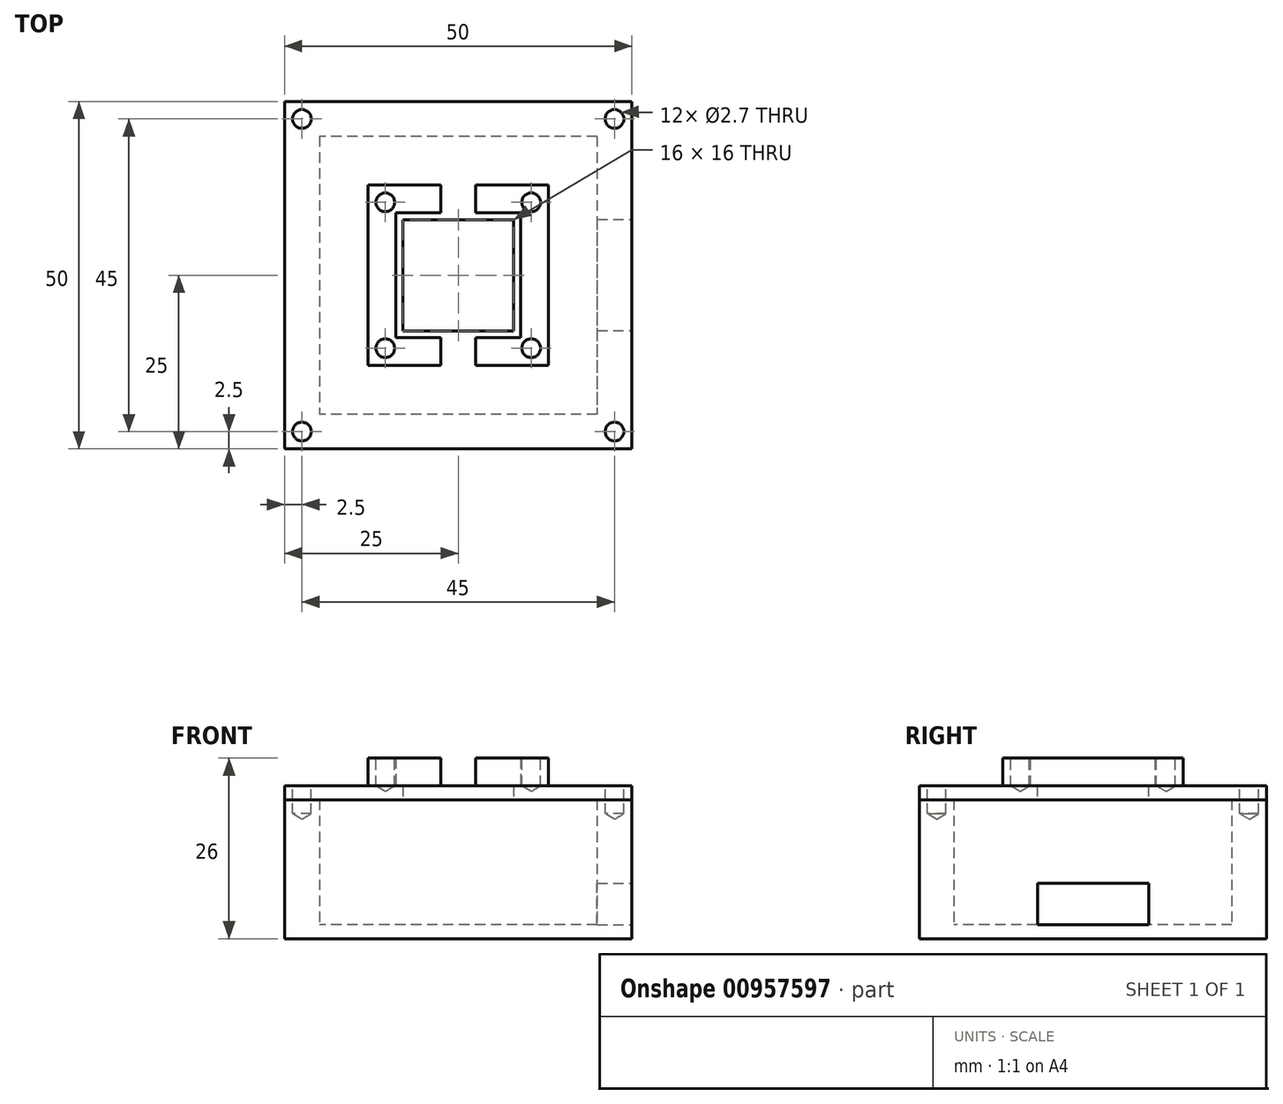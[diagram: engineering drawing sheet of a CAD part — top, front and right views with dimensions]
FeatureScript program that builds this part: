
annotation { "Feature Type Name" : "Feature", "Feature Type Description" : "" }
export const myFeature = defineFeature(function(context is Context, id is Id, definition is map)
    precondition{}
    {
        {
            var Q0;
            Q0=qCreatedBy(makeId("Top.planeOp"),FACE);
            var sketch = newSketch(context, id + "F0", { "sketchPlane" : qUnion([Q0])});
            skLineSegment(sketch, "E0.bottom", {"start": v(20, 20) * mm, "end": v(-20, 20) * mm});
            skLineSegment(sketch, "E0.top", {"start": v(20, -20) * mm, "end": v(-20, -20) * mm});
            skLineSegment(sketch, "E0.left", {"start": v(20, 20) * mm, "end": v(20, -20) * mm});
            skLineSegment(sketch, "E0.right", {"start": v(-20, 20) * mm, "end": v(-20, -20) * mm});
            skPoint(sketch, "E0.middle", {"position": v(0, 0) * mm});
            skLineSegment(sketch, "E1.bottom", {"start": v(25, -25) * mm, "end": v(-25, -25) * mm});
            skLineSegment(sketch, "E1.top", {"start": v(25, 25) * mm, "end": v(-25, 25) * mm});
            skLineSegment(sketch, "E1.left", {"start": v(25, -25) * mm, "end": v(25, 25) * mm});
            skLineSegment(sketch, "E1.right", {"start": v(-25, -25) * mm, "end": v(-25, 25) * mm});
            skSolve(sketch);
        }
        {
            var Q0;
            Q0=makeQuery(id+"F0.imprint","IMPRINT",FACE,{"disambiguationData":[TD([[makeQuery(id+"F0.imprint","IMPRINT",EDGE,{"derivedFrom":sQuery(id+"F0.wireOp",EDGE,"E0.bottom")}),-1.0]])]});
            extrude(context, id + "F1", {"entities" : qUnion([Q0]), "depth" : 18 * mm, "offsetDistance" : 25 * mm});
        }
        {
            var Q0;
            Q0=makeQuery(id+"F0.imprint","IMPRINT",FACE,{"disambiguationData":[TD([[makeQuery(id+"F0.imprint","IMPRINT",EDGE,{"derivedFrom":sQuery(id+"F0.wireOp",EDGE,"E0.bottom")}),-1.0]])]});
            var Q1;
            Q1=makeQuery(id+"F0.imprint","IMPRINT",FACE,{"disambiguationData":[TD([[makeQuery(id+"F0.imprint","IMPRINT",EDGE,{"derivedFrom":sQuery(id+"F0.wireOp",EDGE,"E0.bottom")}),1.0]])]});
            extrude(context, id + "F2", {"entities" : qUnion([Q0, Q1]), "operationType" : NewBodyOperationType.ADD, "oppositeDirection" : true, "depth" : 2 * mm, "offsetDistance" : 25 * mm});
        }
        {
            var Q0;
            {var subQ0=sQuery(id+"F0.wireOp",EDGE,"E1.left");Q0=makeQuery(id+"F2.boolean.opBoolean","MERGE",FACE,{"derivedFrom":[makeQuery(id+"F1.opExtrude","SWEPT_FACE",FACE,{"disambiguationData":[OSD([subQ0])]}),makeQuery(id+"F2.opExtrude","SWEPT_FACE",FACE,{"disambiguationData":[OSD([subQ0])]})]});}
            var sketch = newSketch(context, id + "F3", { "sketchPlane" : qUnion([Q0])});
            skLineSegment(sketch, "E2.bottom", {"start": v(-7.98, 6) * mm, "end": v(8.02, 6) * mm});
            skLineSegment(sketch, "E2.top", {"start": v(-7.98, 0) * mm, "end": v(8.02, 0) * mm});
            skLineSegment(sketch, "E2.left", {"start": v(-7.98, 6) * mm, "end": v(-7.98, 0) * mm});
            skLineSegment(sketch, "E2.right", {"start": v(8.02, 6) * mm, "end": v(8.02, 0) * mm});
            skLineSegment(sketch, "E3", {"start": v(-7.98, -2) * mm, "end": v(-7.98, 8) * mm, "construction": true});
            skLineSegment(sketch, "E4", {"start": v(8.02, -2) * mm, "end": v(8.02, 8) * mm, "construction": true});
            skLineSegment(sketch, "E5", {"start": v(-25, 6) * mm, "end": v(-7.98, 6) * mm, "construction": true});
            skLineSegment(sketch, "E6", {"start": v(8.02, 6) * mm, "end": v(25, 6) * mm, "construction": true});
            skSolve(sketch);
        }
        {
            var Q0;
            Q0=makeQuery(id+"F3.imprint","IMPRINT",FACE,{"disambiguationData":[TD([[makeQuery(id+"F3.imprint","IMPRINT",EDGE,{"derivedFrom":sQuery(id+"F3.wireOp",EDGE,"E2.bottom")}),-1.0]])]});
            extrude(context, id + "F4", {"entities" : qUnion([Q0]), "operationType" : NewBodyOperationType.REMOVE, "endBound" : BoundingType.UP_TO_NEXT, "oppositeDirection" : true, "depth" : 25 * mm, "offsetDistance" : 25 * mm});
        }
        {
            var Q0;
            Q0=makeQuery(id+"F1.opExtrude","CAP_FACE",FACE,{"disambiguationData":[OSD([sQuery(id+"F0.wireOp",EDGE,"E0.bottom"),sQuery(id+"F0.wireOp",EDGE,"E0.top"),sQuery(id+"F0.wireOp",EDGE,"E0.left"),sQuery(id+"F0.wireOp",EDGE,"E0.right"),sQuery(id+"F0.wireOp",EDGE,"E1.bottom"),sQuery(id+"F0.wireOp",EDGE,"E1.top"),sQuery(id+"F0.wireOp",EDGE,"E1.left"),sQuery(id+"F0.wireOp",EDGE,"E1.right")])],"isStart":false});
            var sketch = newSketch(context, id + "F5", { "sketchPlane" : qUnion([Q0])});
            skLineSegment(sketch, "E7.bottom", {"start": v(-25, -25) * mm, "end": v(25, -25) * mm});
            skLineSegment(sketch, "E7.top", {"start": v(-25, 25) * mm, "end": v(25, 25) * mm});
            skLineSegment(sketch, "E7.left", {"start": v(-25, -25) * mm, "end": v(-25, 25) * mm});
            skLineSegment(sketch, "E7.right", {"start": v(25, -25) * mm, "end": v(25, 25) * mm});
            skLineSegment(sketch, "E8.bottom", {"start": v(8, -8) * mm, "end": v(-8, -8) * mm});
            skLineSegment(sketch, "E8.top", {"start": v(8, 8) * mm, "end": v(-8, 8) * mm});
            skLineSegment(sketch, "E8.left", {"start": v(8, -8) * mm, "end": v(8, 8) * mm});
            skLineSegment(sketch, "E8.right", {"start": v(-8, -8) * mm, "end": v(-8, 8) * mm});
            skPoint(sketch, "E8.middle", {"position": v(0, 0) * mm});
            skSolve(sketch);
        }
        {
            var Q0;
            Q0=makeQuery(id+"F5.imprint","IMPRINT",FACE,{"disambiguationData":[TD([[makeQuery(id+"F5.imprint","IMPRINT",EDGE,{"derivedFrom":sQuery(id+"F5.wireOp",EDGE,"E8.bottom")}),1.0]])]});
            var Q1;
            Q1=makeQuery(id+"F5.imprint","IMPRINT",FACE,{"disambiguationData":[TD([[makeQuery(id+"F5.imprint","IMPRINT",EDGE,{"derivedFrom":sQuery(id+"F5.wireOp",EDGE,"E7.bottom")}),-1.0]])]});
            extrude(context, id + "F6", {"entities" : qUnion([Q0, Q1]), "depth" : 2 * mm, "offsetDistance" : 25 * mm});
        }
        {
            var Q0;
            Q0=makeQuery(id+"F6.opExtrude","CAP_FACE",FACE,{"disambiguationData":[OSD([sQuery(id+"F5.wireOp",EDGE,"E7.bottom"),sQuery(id+"F5.wireOp",EDGE,"E7.top"),sQuery(id+"F5.wireOp",EDGE,"E7.left"),sQuery(id+"F5.wireOp",EDGE,"E7.right"),sQuery(id+"F5.wireOp",EDGE,"E8.bottom"),sQuery(id+"F5.wireOp",EDGE,"E8.top"),sQuery(id+"F5.wireOp",EDGE,"E8.left"),sQuery(id+"F5.wireOp",EDGE,"E8.right")])],"isStart":false});
            var sketch = newSketch(context, id + "F7", { "sketchPlane" : qUnion([Q0])});
            skLineSegment(sketch, "E9.bottom", {"start": v(-9, 9) * mm, "end": v(9, 9) * mm});
            skLineSegment(sketch, "E9.top", {"start": v(-9, -9) * mm, "end": v(9, -9) * mm});
            skLineSegment(sketch, "E9.left", {"start": v(-9, 9) * mm, "end": v(-9, -9) * mm});
            skLineSegment(sketch, "E9.right", {"start": v(9, 9) * mm, "end": v(9, -9) * mm});
            skPoint(sketch, "E9.middle", {"position": v(0, 0) * mm});
            skLineSegment(sketch, "E10.bottom", {"start": v(13, 13) * mm, "end": v(-13, 13) * mm});
            skLineSegment(sketch, "E10.top", {"start": v(13, -13) * mm, "end": v(-13, -13) * mm});
            skLineSegment(sketch, "E10.left", {"start": v(13, 13) * mm, "end": v(13, -13) * mm});
            skLineSegment(sketch, "E10.right", {"start": v(-13, 13) * mm, "end": v(-13, -13) * mm});
            skSolve(sketch);
        }
        {
            var Q0;
            Q0=makeQuery(id+"F7.imprint","IMPRINT",FACE,{"disambiguationData":[TD([[makeQuery(id+"F7.imprint","IMPRINT",EDGE,{"derivedFrom":sQuery(id+"F7.wireOp",EDGE,"E9.bottom")}),1.0]])]});
            extrude(context, id + "F8", {"entities" : qUnion([Q0]), "operationType" : NewBodyOperationType.ADD, "depth" : 4 * mm, "offsetDistance" : 25 * mm});
        }
        {
            var Q0;
            Q0=makeQuery(id+"F8.opExtrude","CAP_FACE",FACE,{"disambiguationData":[OSD([sQuery(id+"F7.wireOp",EDGE,"E9.bottom"),sQuery(id+"F7.wireOp",EDGE,"E9.top"),sQuery(id+"F7.wireOp",EDGE,"E9.left"),sQuery(id+"F7.wireOp",EDGE,"E9.right"),sQuery(id+"F7.wireOp",EDGE,"E10.bottom"),sQuery(id+"F7.wireOp",EDGE,"E10.top"),sQuery(id+"F7.wireOp",EDGE,"E10.left"),sQuery(id+"F7.wireOp",EDGE,"E10.right")])],"isStart":false});
            var sketch = newSketch(context, id + "F9", { "sketchPlane" : qUnion([Q0])});
            skLineSegment(sketch, "E11", {"start": v(-2.5, 13) * mm, "end": v(-2.5, 9) * mm});
            skLineSegment(sketch, "E12.MirrorCS", {"start": v(2.5, 13) * mm, "end": v(2.5, 9) * mm});
            skLineSegment(sketch, "E13.MirrorCS", {"start": v(2.5, -13) * mm, "end": v(2.5, -9) * mm});
            skLineSegment(sketch, "E14.MirrorCS", {"start": v(-2.5, -13) * mm, "end": v(-2.5, -9) * mm});
            skLineSegment(sketch, "E15", {"start": v(-13, 13) * mm, "end": v(-9, 9) * mm, "construction": true});
            skPoint(sketch, "E16", {"position": v(-10.5, 10.5) * mm});
            skPoint(sketch, "E17.MirrorP", {"position": v(10.5, 10.5) * mm});
            skLineSegment(sketch, "E18.MirrorCS", {"start": v(13, 13) * mm, "end": v(9, 9) * mm, "construction": true});
            skLineSegment(sketch, "E19.MirrorCS", {"start": v(-13, -13) * mm, "end": v(-9, -9) * mm, "construction": true});
            skPoint(sketch, "E20.MirrorP", {"position": v(-10.5, -10.5) * mm});
            skLineSegment(sketch, "E21.MirrorCS", {"start": v(13, -13) * mm, "end": v(9, -9) * mm, "construction": true});
            skPoint(sketch, "E22.MirrorP", {"position": v(10.5, -10.5) * mm});
            skSolve(sketch);
        }
        {
            var Q0;
            Q0=sQuery(id+"F9.wireOp",VERTEX,"E16");
            var Q1;
            Q1=sQuery(id+"F9.wireOp",VERTEX,"E17.MirrorP");
            var Q2;
            Q2=sQuery(id+"F9.wireOp",VERTEX,"E20.MirrorP");
            var Q3;
            Q3=sQuery(id+"F9.wireOp",VERTEX,"E22.MirrorP");
            var Q4;
            Q4=makeQuery(id+"F6.opExtrude","SWEPT_BODY",BODY,{"disambiguationData":[OSD([sQuery(id+"F5.wireOp",EDGE,"E7.bottom"),sQuery(id+"F5.wireOp",EDGE,"E7.top"),sQuery(id+"F5.wireOp",EDGE,"E7.left"),sQuery(id+"F5.wireOp",EDGE,"E7.right"),sQuery(id+"F5.wireOp",EDGE,"E8.bottom"),sQuery(id+"F5.wireOp",EDGE,"E8.top"),sQuery(id+"F5.wireOp",EDGE,"E8.left"),sQuery(id+"F5.wireOp",EDGE,"E8.right")])]});
            hole(context, id + "F10", {"style" : HoleStyle.SIMPLE, "endStyle" : HoleEndStyle.BLIND, "standardTappedOrClearance" : lookupTablePath({ "standard" : "ISO", "engagement" : "50%", "pitch" : "0.5 mm", "size" : "M3", "type" : "Tapped" }), "standardBlindInLast" : lookupTablePath({ "standard" : "ISO", "fit" : "Normal", "engagement" : "50%", "pitch" : "0.5 mm", "size" : "M3", "type" : "Clearance & tapped" }), "holeDiameter" : 2.7 * mm, "majorDiameter" : 3 * mm, "showTappedDepth" : true, "holeDepth" : 4 * mm, "isTappedThrough" : true, "tappedDepth" : 2.5 * mm, "tapClearance" : 3, "locations" : qUnion([Q0, Q1, Q2, Q3]), "scope" : qUnion([Q4])});
        }
        {
            var Q0;
            {var subQ0=sQuery(id+"F9.wireOp",EDGE,"E11");Q0=makeQuery(id+"F9.imprint","IMPRINT",FACE,{"disambiguationData":[TD([[makeQuery(id+"F9.imprint","IMPRINT",EDGE,{"derivedFrom":subQ0}),1.0]])]});}
            var Q1;
            {var subQ0=sQuery(id+"F9.wireOp",EDGE,"E13.MirrorCS");Q1=makeQuery(id+"F9.imprint","IMPRINT",FACE,{"disambiguationData":[TD([[makeQuery(id+"F9.imprint","IMPRINT",EDGE,{"derivedFrom":subQ0}),1.0]])]});}
            var Q2;
            {var subQ0=sQuery(id+"F5.wireOp",EDGE,"E7.left");var subQ1=sQuery(id+"F5.wireOp",EDGE,"E7.top");var subQ2=sQuery(id+"F5.wireOp",EDGE,"E7.right");var subQ3=sQuery(id+"F5.wireOp",EDGE,"E7.bottom");Q2=makeQuery(id+"F8.boolean.opBoolean","SPLIT",FACE,{"disambiguationData":[TD([makeQuery(id+"F6.opExtrude","SWEPT_FACE",FACE,{"disambiguationData":[OSD([subQ3])]})])],"derivedFrom":makeQuery(id+"F6.opExtrude","CAP_FACE",FACE,{"disambiguationData":[OSD([subQ3,subQ1,subQ0,subQ2,sQuery(id+"F5.wireOp",EDGE,"E8.bottom"),sQuery(id+"F5.wireOp",EDGE,"E8.top"),sQuery(id+"F5.wireOp",EDGE,"E8.left"),sQuery(id+"F5.wireOp",EDGE,"E8.right")])],"isStart":false})});}
            extrude(context, id + "F11", {"entities" : qUnion([Q0, Q1]), "operationType" : NewBodyOperationType.REMOVE, "endBound" : BoundingType.UP_TO_SURFACE, "oppositeDirection" : true, "depth" : 25 * mm, "endBoundEntityFace" : qUnion([Q2]), "offsetDistance" : 25 * mm});
        }
        {
            var Q0;
            {var subQ0=sQuery(id+"F7.wireOp",EDGE,"E10.top");var subQ1=sQuery(id+"F7.wireOp",EDGE,"E9.top");var subQ2=sQuery(id+"F7.wireOp",EDGE,"E10.bottom");var subQ3=sQuery(id+"F7.wireOp",EDGE,"E9.bottom");var subQ4=sQuery(id+"F5.wireOp",EDGE,"E8.right");var subQ5=sQuery(id+"F5.wireOp",EDGE,"E8.left");var subQ6=sQuery(id+"F5.wireOp",EDGE,"E8.top");var subQ7=sQuery(id+"F5.wireOp",EDGE,"E8.bottom");var subQ8=sQuery(id+"F5.wireOp",EDGE,"E7.right");var subQ9=sQuery(id+"F5.wireOp",EDGE,"E7.left");var subQ10=sQuery(id+"F5.wireOp",EDGE,"E7.top");var subQ11=sQuery(id+"F5.wireOp",EDGE,"E7.bottom");var subQ12=makeQuery(id+"F6.opExtrude","CAP_FACE",FACE,{"disambiguationData":[OSD([subQ11,subQ10,subQ9,subQ8,subQ7,subQ6,subQ5,subQ4])],"isStart":false});Q0=makeQuery(id+"F11.boolean.opBoolean","MERGE",FACE,{"derivedFrom":[makeQuery(id+"F8.boolean.opBoolean","SPLIT",FACE,{"disambiguationData":[TD([makeQuery(id+"F6.opExtrude","SWEPT_FACE",FACE,{"disambiguationData":[OSD([subQ11])]})])],"derivedFrom":subQ12}),makeQuery(id+"F8.boolean.opBoolean","SPLIT",FACE,{"disambiguationData":[TD([makeQuery(id+"F6.opExtrude","SWEPT_FACE",FACE,{"disambiguationData":[OSD([subQ7])]})])],"derivedFrom":subQ12})],"fromTools":[makeQuery(id+"F11.opExtrude","CAP_FACE",FACE,{"disambiguationData":[OSD([subQ3,subQ2,sQuery(id+"F9.wireOp",EDGE,"E11"),sQuery(id+"F9.wireOp",EDGE,"E12.MirrorCS")])],"isStart":false}),makeQuery(id+"F11.opExtrude","CAP_FACE",FACE,{"disambiguationData":[OSD([subQ1,subQ0,sQuery(id+"F9.wireOp",EDGE,"E13.MirrorCS"),sQuery(id+"F9.wireOp",EDGE,"E14.MirrorCS")])],"isStart":false})]});}
            var sketch = newSketch(context, id + "F12", { "sketchPlane" : qUnion([Q0])});
            skLineSegment(sketch, "E23", {"start": v(-25, 25) * mm, "end": v(-20, 20) * mm, "construction": true});
            skPoint(sketch, "E24", {"position": v(-22.5, 22.5) * mm});
            skLineSegment(sketch, "E25.MirrorCS", {"start": v(25, 25) * mm, "end": v(20, 20) * mm, "construction": true});
            skPoint(sketch, "E26.MirrorP", {"position": v(22.5, 22.5) * mm});
            skLineSegment(sketch, "E27.MirrorCS", {"start": v(25, -25) * mm, "end": v(20, -20) * mm, "construction": true});
            skPoint(sketch, "E28.MirrorP", {"position": v(22.5, -22.5) * mm});
            skLineSegment(sketch, "E29.MirrorCS", {"start": v(-25, -25) * mm, "end": v(-20, -20) * mm, "construction": true});
            skPoint(sketch, "E30.MirrorP", {"position": v(-22.5, -22.5) * mm});
            skSolve(sketch);
        }
        {
            var Q0;
            Q0=sQuery(id+"F12.wireOp",VERTEX,"E24");
            var Q1;
            Q1=sQuery(id+"F12.wireOp",VERTEX,"E26.MirrorP");
            var Q2;
            Q2=sQuery(id+"F12.wireOp",VERTEX,"E30.MirrorP");
            var Q3;
            Q3=sQuery(id+"F12.wireOp",VERTEX,"E28.MirrorP");
            var Q4;
            Q4=makeQuery(id+"F1.opExtrude","SWEPT_BODY",BODY,{"disambiguationData":[OSD([sQuery(id+"F0.wireOp",EDGE,"E0.bottom"),sQuery(id+"F0.wireOp",EDGE,"E0.top"),sQuery(id+"F0.wireOp",EDGE,"E0.left"),sQuery(id+"F0.wireOp",EDGE,"E0.right"),sQuery(id+"F0.wireOp",EDGE,"E1.bottom"),sQuery(id+"F0.wireOp",EDGE,"E1.top"),sQuery(id+"F0.wireOp",EDGE,"E1.left"),sQuery(id+"F0.wireOp",EDGE,"E1.right")])]});
            var Q5;
            Q5=makeQuery(id+"F6.opExtrude","SWEPT_BODY",BODY,{"disambiguationData":[OSD([sQuery(id+"F5.wireOp",EDGE,"E7.bottom"),sQuery(id+"F5.wireOp",EDGE,"E7.top"),sQuery(id+"F5.wireOp",EDGE,"E7.left"),sQuery(id+"F5.wireOp",EDGE,"E7.right"),sQuery(id+"F5.wireOp",EDGE,"E8.bottom"),sQuery(id+"F5.wireOp",EDGE,"E8.top"),sQuery(id+"F5.wireOp",EDGE,"E8.left"),sQuery(id+"F5.wireOp",EDGE,"E8.right")])]});
            hole(context, id + "F13", {"style" : HoleStyle.SIMPLE, "endStyle" : HoleEndStyle.BLIND, "standardTappedOrClearance" : lookupTablePath({ "standard" : "ISO", "engagement" : "50%", "pitch" : "0.5 mm", "size" : "M3", "type" : "Tapped" }), "standardBlindInLast" : lookupTablePath({ "standard" : "ISO", "fit" : "Normal", "engagement" : "50%", "pitch" : "0.5 mm", "size" : "M3", "type" : "Clearance & tapped" }), "holeDiameter" : 2.7 * mm, "majorDiameter" : 3 * mm, "showTappedDepth" : true, "holeDepth" : 4 * mm, "isTappedThrough" : true, "tappedDepth" : 2.5 * mm, "tapClearance" : 3, "locations" : qUnion([Q0, Q1, Q2, Q3]), "scope" : qUnion([Q4, Q5])});
        }
    });
